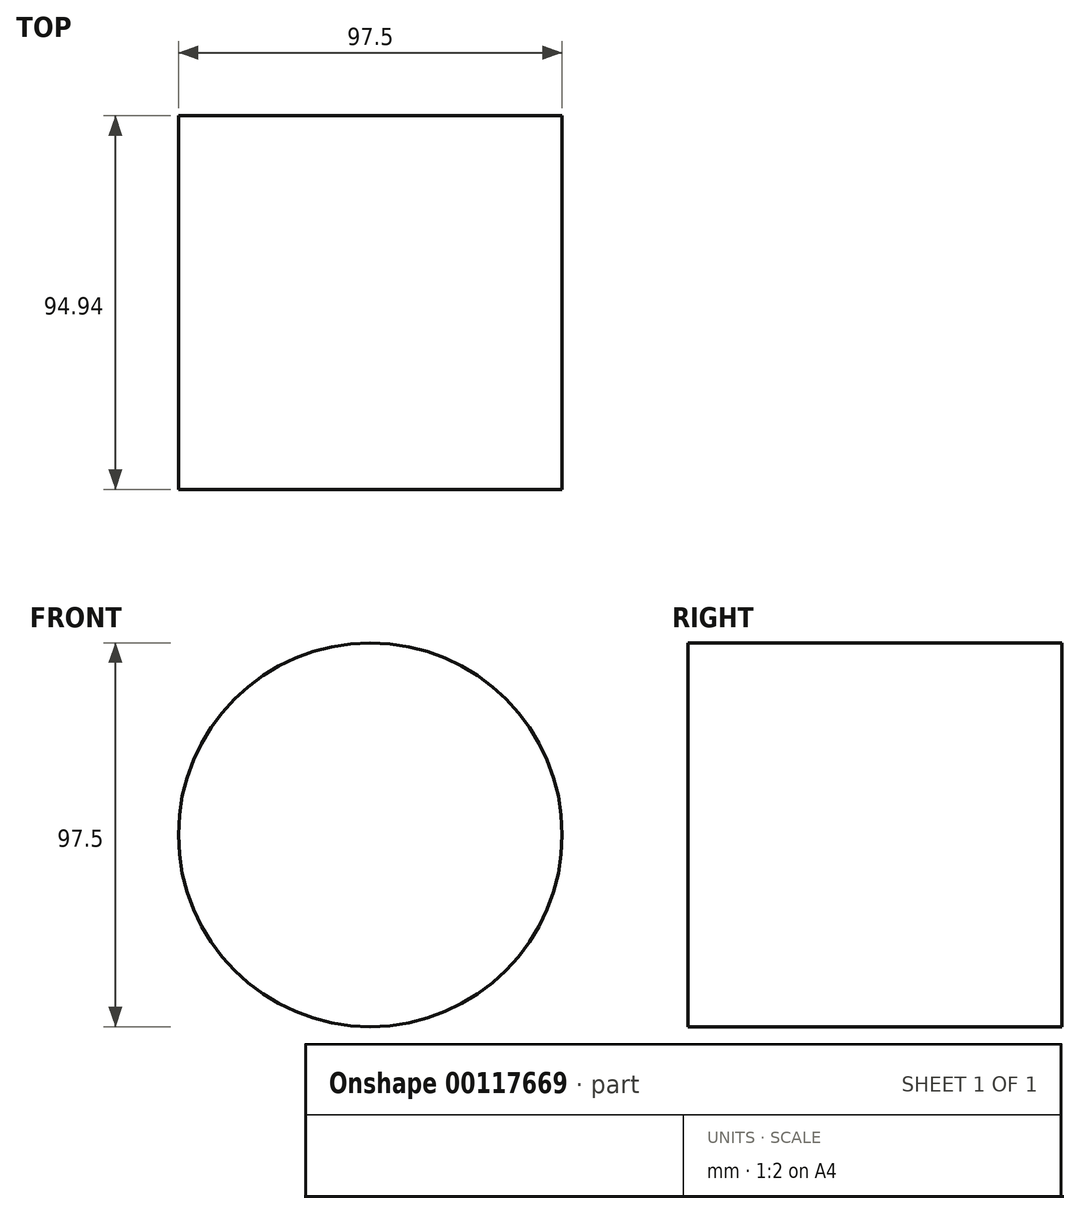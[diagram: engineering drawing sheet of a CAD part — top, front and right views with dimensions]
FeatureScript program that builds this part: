
annotation { "Feature Type Name" : "Feature", "Feature Type Description" : "" }
export const myFeature = defineFeature(function(context is Context, id is Id, definition is map)
    precondition{}
    {
        {
            var Q0;
            Q0=qCreatedBy(makeId("Front.planeOp"),FACE);
            var sketch = newSketch(context, id + "F0", { "sketchPlane" : qUnion([Q0])});
            skCircle(sketch, "E0", {"center": v(0, 0) * mm, "radius": 48.75 * mm});
            skSolve(sketch);
        }
        {
            var Q0;
            Q0 = qSketchRegion(id + "F0", true);
            extrude(context, id + "F1", {"entities" : qUnion([Q0]), "oppositeDirection" : true, "depth" : 94.94 * mm});
        }
    });
